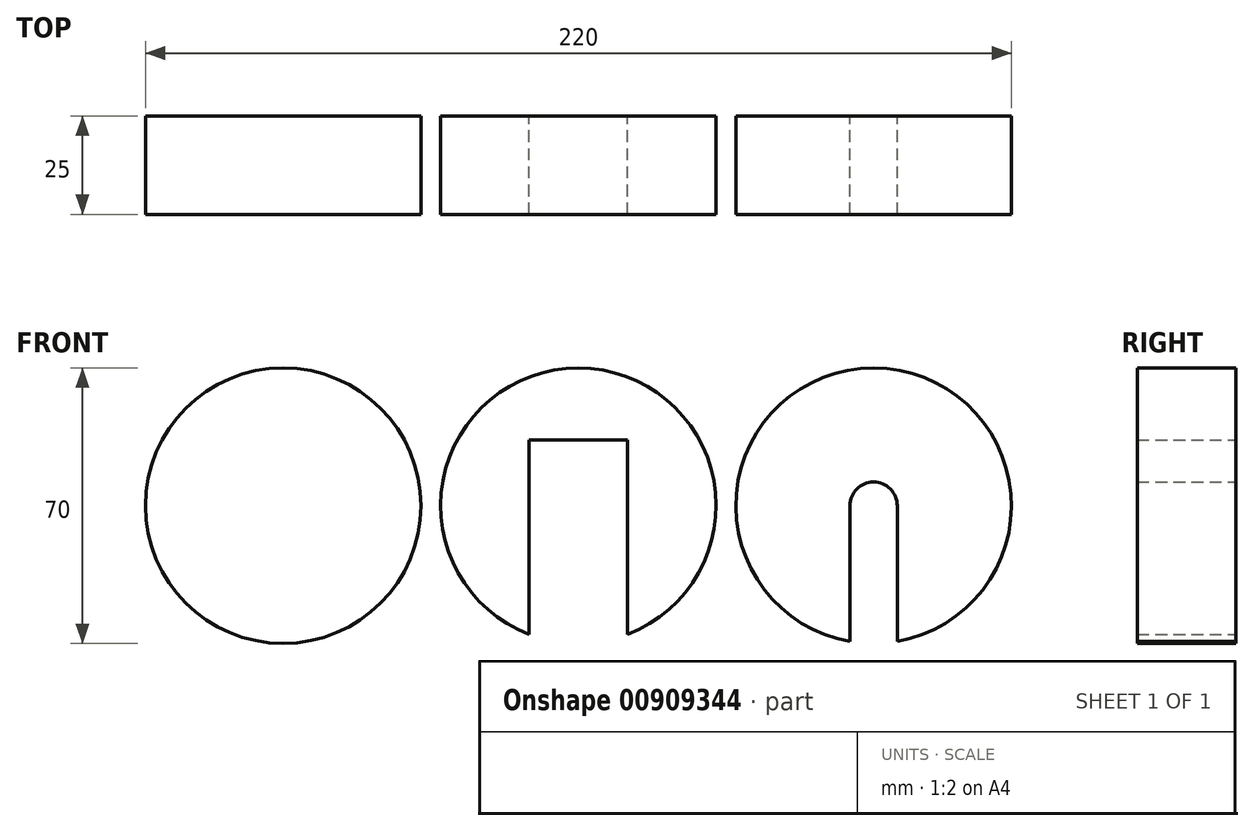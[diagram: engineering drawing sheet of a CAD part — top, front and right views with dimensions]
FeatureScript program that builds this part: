
annotation { "Feature Type Name" : "Feature", "Feature Type Description" : "" }
export const myFeature = defineFeature(function(context is Context, id is Id, definition is map)
    precondition{}
    {
        {
            var Q0;
            Q0=qCreatedBy(makeId("Front.planeOp"),FACE);
            var sketch = newSketch(context, id + "F0", { "sketchPlane" : qUnion([Q0])});
            skCircle(sketch, "E0", {"center": v(-75, 0) * mm, "radius": 35 * mm});
            skArc(sketch, "E1", {"start": v(81, -34.48) * mm, "mid": v(75, 35) * mm, "end": v(69, -34.48) * mm});
            skArc(sketch, "E2", {"start": v(12.5, -32.7) * mm, "mid": v(0, 35) * mm, "end": v(-12.5, -32.7) * mm});
            skLineSegment(sketch, "E3.bottom", {"start": v(12.5, 16.75) * mm, "end": v(-12.5, 16.75) * mm});
            skLineSegment(sketch, "E3.left", {"start": v(12.5, 16.75) * mm, "end": v(12.5, -16.75) * mm});
            skLineSegment(sketch, "E3.right", {"start": v(-12.5, 16.75) * mm, "end": v(-12.5, -16.75) * mm});
            skLineSegment(sketch, "E4", {"start": v(-12.5, -16.75) * mm, "end": v(-12.5, -32.7) * mm});
            skLineSegment(sketch, "E5", {"start": v(12.5, -32.7) * mm, "end": v(12.5, -16.75) * mm});
            skArc(sketch, "E6", {"start": v(81, 0) * mm, "mid": v(75, 6) * mm, "end": v(69, 0) * mm});
            skLineSegment(sketch, "E7", {"start": v(69, 0) * mm, "end": v(69, -34.48) * mm});
            skLineSegment(sketch, "E8", {"start": v(81, -34.48) * mm, "end": v(81, 0) * mm});
            skPoint(sketch, "E9.orphan", {"position": v(69, 0) * mm});
            skSolve(sketch);
        }
        {
            var Q0;
            Q0 = qSketchRegion(id + "F0", true);
            extrude(context, id + "F1", {"entities" : qUnion([Q0]), "depth" : 25 * mm, "offsetDistance" : 25 * mm});
        }
    });
